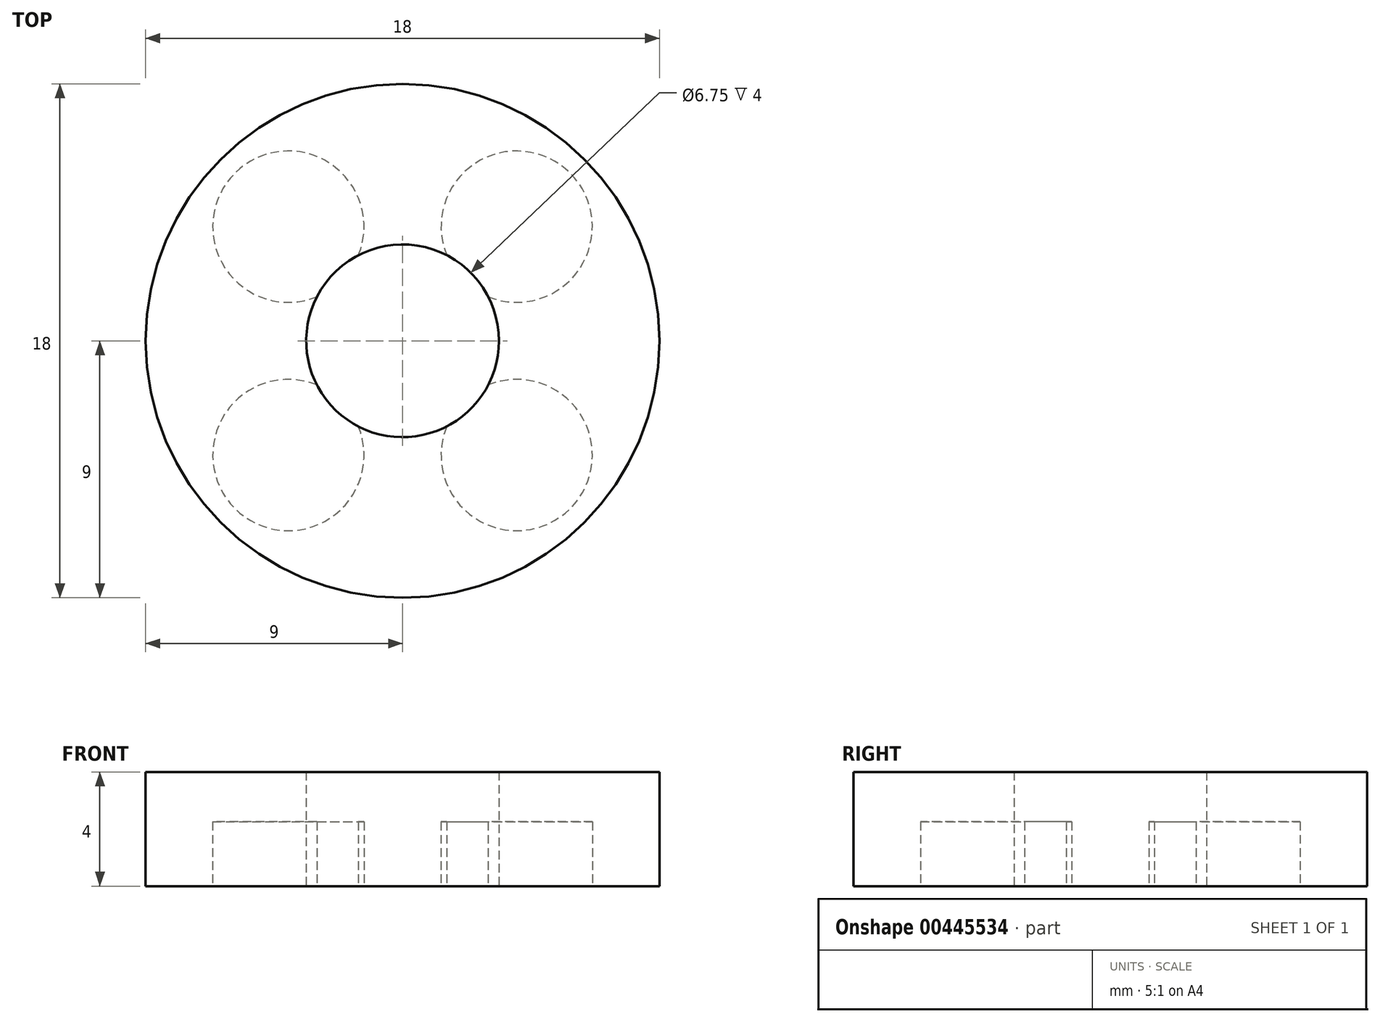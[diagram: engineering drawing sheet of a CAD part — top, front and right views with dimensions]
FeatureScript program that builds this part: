
annotation { "Feature Type Name" : "Feature", "Feature Type Description" : "" }
export const myFeature = defineFeature(function(context is Context, id is Id, definition is map)
    precondition{}
    {
        {
            var Q0;
            Q0=qCreatedBy(makeId("Top.planeOp"),FACE);
            var sketch = newSketch(context, id + "F0", { "sketchPlane" : qUnion([Q0])});
            skCircle(sketch, "E0", {"center": v(0, 0) * mm, "radius": 9 * mm});
            skCircle(sketch, "E1", {"center": v(0, 0) * mm, "radius": 3.38 * mm});
            skCircle(sketch, "E2", {"center": v(-4, 4) * mm, "radius": 2.65 * mm});
            skCircle(sketch, "E3.MirrorC", {"center": v(4, 4) * mm, "radius": 2.65 * mm});
            skCircle(sketch, "E4.MirrorC", {"center": v(4, -4) * mm, "radius": 2.65 * mm});
            skCircle(sketch, "E5.MirrorC", {"center": v(-4, -4) * mm, "radius": 2.65 * mm});
            skSolve(sketch);
        }
        {
            var Q0;
            Q0=makeQuery(id+"F0.imprint","IMPRINT",FACE,{"disambiguationData":[TD([[makeQuery(id+"F0.imprint","IMPRINT",EDGE,{"derivedFrom":sQuery(id+"F0.wireOp",EDGE,"E0")}),1.0]])]});
            var Q1;
            {var subQ0=sQuery(id+"F0.wireOp",EDGE,"E5.MirrorC");var subQ1=sQuery(id+"F0.wireOp",EDGE,"E1");var subQ2=makeQuery(id+"F0.imprint","INTERSECT",VERTEX,{"disambiguationData":[OD(0.0)],"derivedFrom":[subQ1,subQ0]});Q1=makeQuery(id+"F0.imprint","IMPRINT",FACE,{"disambiguationData":[TD([[makeQuery(id+"F0.imprint","IMPRINT",EDGE,{"disambiguationData":[TD([[subQ2,-1.0]])],"derivedFrom":subQ1}),-1.0]])]});}
            var Q2;
            {var subQ0=sQuery(id+"F0.wireOp",EDGE,"E4.MirrorC");var subQ1=sQuery(id+"F0.wireOp",EDGE,"E1");var subQ2=makeQuery(id+"F0.imprint","INTERSECT",VERTEX,{"disambiguationData":[OD(0.0)],"derivedFrom":[subQ1,subQ0]});Q2=makeQuery(id+"F0.imprint","IMPRINT",FACE,{"disambiguationData":[TD([[makeQuery(id+"F0.imprint","IMPRINT",EDGE,{"disambiguationData":[TD([[subQ2,-1.0]])],"derivedFrom":subQ1}),-1.0]])]});}
            var Q3;
            {var subQ0=sQuery(id+"F0.wireOp",EDGE,"E3.MirrorC");var subQ1=sQuery(id+"F0.wireOp",EDGE,"E1");var subQ2=makeQuery(id+"F0.imprint","INTERSECT",VERTEX,{"disambiguationData":[OD(0.0)],"derivedFrom":[subQ1,subQ0]});Q3=makeQuery(id+"F0.imprint","IMPRINT",FACE,{"disambiguationData":[TD([[makeQuery(id+"F0.imprint","IMPRINT",EDGE,{"disambiguationData":[TD([[subQ2,1.0]])],"derivedFrom":subQ1}),-1.0]])]});}
            var Q4;
            {var subQ0=sQuery(id+"F0.wireOp",EDGE,"E2");var subQ1=sQuery(id+"F0.wireOp",EDGE,"E1");var subQ2=makeQuery(id+"F0.imprint","INTERSECT",VERTEX,{"disambiguationData":[OD(0.0)],"derivedFrom":[subQ1,subQ0]});Q4=makeQuery(id+"F0.imprint","IMPRINT",FACE,{"disambiguationData":[TD([[makeQuery(id+"F0.imprint","IMPRINT",EDGE,{"disambiguationData":[TD([[subQ2,-1.0]])],"derivedFrom":subQ1}),-1.0]])]});}
            extrude(context, id + "F1", {"entities" : qUnion([Q0, Q1, Q2, Q3, Q4]), "depth" : 4 * mm});
        }
        {
            var Q0;
            {var subQ0=sQuery(id+"F0.wireOp",EDGE,"E5.MirrorC");var subQ1=sQuery(id+"F0.wireOp",EDGE,"E1");var subQ2=makeQuery(id+"F0.imprint","INTERSECT",VERTEX,{"disambiguationData":[OD(0.0)],"derivedFrom":[subQ1,subQ0]});Q0=makeQuery(id+"F0.imprint","IMPRINT",FACE,{"disambiguationData":[TD([[makeQuery(id+"F0.imprint","IMPRINT",EDGE,{"disambiguationData":[TD([[subQ2,-1.0]])],"derivedFrom":subQ1}),-1.0]])]});}
            var Q1;
            {var subQ0=sQuery(id+"F0.wireOp",EDGE,"E4.MirrorC");var subQ1=sQuery(id+"F0.wireOp",EDGE,"E1");var subQ2=makeQuery(id+"F0.imprint","INTERSECT",VERTEX,{"disambiguationData":[OD(0.0)],"derivedFrom":[subQ1,subQ0]});Q1=makeQuery(id+"F0.imprint","IMPRINT",FACE,{"disambiguationData":[TD([[makeQuery(id+"F0.imprint","IMPRINT",EDGE,{"disambiguationData":[TD([[subQ2,-1.0]])],"derivedFrom":subQ1}),-1.0]])]});}
            var Q2;
            {var subQ0=sQuery(id+"F0.wireOp",EDGE,"E3.MirrorC");var subQ1=sQuery(id+"F0.wireOp",EDGE,"E1");var subQ2=makeQuery(id+"F0.imprint","INTERSECT",VERTEX,{"disambiguationData":[OD(0.0)],"derivedFrom":[subQ1,subQ0]});Q2=makeQuery(id+"F0.imprint","IMPRINT",FACE,{"disambiguationData":[TD([[makeQuery(id+"F0.imprint","IMPRINT",EDGE,{"disambiguationData":[TD([[subQ2,1.0]])],"derivedFrom":subQ1}),-1.0]])]});}
            var Q3;
            {var subQ0=sQuery(id+"F0.wireOp",EDGE,"E2");var subQ1=sQuery(id+"F0.wireOp",EDGE,"E1");var subQ2=makeQuery(id+"F0.imprint","INTERSECT",VERTEX,{"disambiguationData":[OD(0.0)],"derivedFrom":[subQ1,subQ0]});Q3=makeQuery(id+"F0.imprint","IMPRINT",FACE,{"disambiguationData":[TD([[makeQuery(id+"F0.imprint","IMPRINT",EDGE,{"disambiguationData":[TD([[subQ2,-1.0]])],"derivedFrom":subQ1}),-1.0]])]});}
            extrude(context, id + "F2", {"entities" : qUnion([Q0, Q1, Q2, Q3]), "operationType" : NewBodyOperationType.REMOVE, "depth" : 2.25 * mm});
        }
    });
